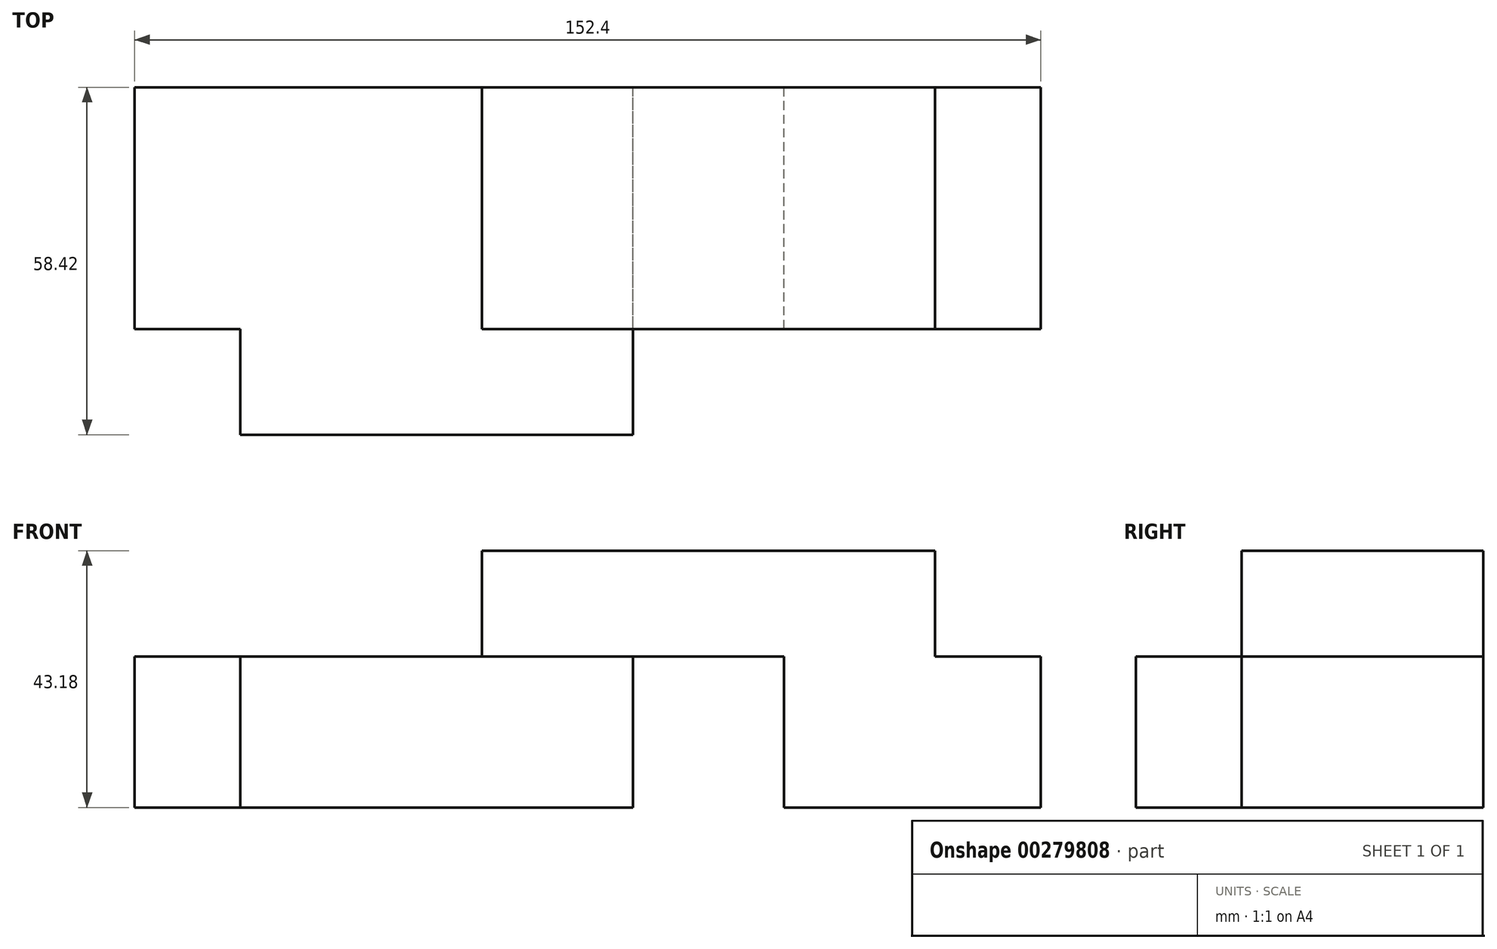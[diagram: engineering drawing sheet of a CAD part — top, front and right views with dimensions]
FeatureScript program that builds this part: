
annotation { "Feature Type Name" : "Feature", "Feature Type Description" : "" }
export const myFeature = defineFeature(function(context is Context, id is Id, definition is map)
    precondition{}
    {
        {
            var Q0;
            Q0=qCreatedBy(makeId("Right.planeOp"),FACE);
            var sketch = newSketch(context, id + "F0", { "sketchPlane" : qUnion([Q0])});
            skLineSegment(sketch, "E0.bottom", {"start": v(16.45, 25.4) * mm, "end": v(57.09, 25.4) * mm});
            skLineSegment(sketch, "E0.top", {"start": v(16.45, 0) * mm, "end": v(57.09, 0) * mm});
            skLineSegment(sketch, "E0.left", {"start": v(16.45, 25.4) * mm, "end": v(16.45, 0) * mm});
            skLineSegment(sketch, "E0.right", {"start": v(57.09, 25.4) * mm, "end": v(57.09, 0) * mm});
            skSolve(sketch);
        }
        {
            var Q0;
            Q0=makeQuery(id+"F0.imprint","IMPRINT",FACE,{"disambiguationData":[TD([[makeQuery(id+"F0.imprint","IMPRINT",EDGE,{"derivedFrom":sQuery(id+"F0.wireOp",EDGE,"E0.bottom")}),-1.0]])]});
            extrude(context, id + "F1", {"entities" : qUnion([Q0]), "depth" : 17.78 * mm});
        }
        {
            var Q0;
            Q0=makeQuery(id+"F1.opExtrude","CAP_FACE",FACE,{"disambiguationData":[OSD([sQuery(id+"F0.wireOp",EDGE,"E0.bottom"),sQuery(id+"F0.wireOp",EDGE,"E0.top"),sQuery(id+"F0.wireOp",EDGE,"E0.left"),sQuery(id+"F0.wireOp",EDGE,"E0.right")])],"isStart":true});
            extrude(context, id + "F2", {"entities" : qUnion([Q0]), "operationType" : NewBodyOperationType.ADD, "depth" : 25.4 * mm});
        }
        {
            var Q0;
            {var subQ0=sQuery(id+"F0.wireOp",EDGE,"E0.bottom");Q0=makeQuery(id+"F2.boolean.opBoolean","MERGE",FACE,{"derivedFrom":[makeQuery(id+"F1.opExtrude","SWEPT_FACE",FACE,{"disambiguationData":[OSD([subQ0])]}),makeQuery(id+"F2.opExtrude","SWEPT_FACE",FACE,{"disambiguationData":[OSD([subQ0])]})]});}
            var sketch = newSketch(context, id + "F3", { "sketchPlane" : qUnion([Q0])});
            skLineSegment(sketch, "E1", {"start": v(0, 57.09) * mm, "end": v(0, 16.45) * mm});
            skSolve(sketch);
        }
        {
            var Q0;
            {var subQ0=sQuery(id+"F3.wireOp",EDGE,"E1");Q0=makeQuery(id+"F3.imprint","IMPRINT",FACE,{"disambiguationData":[TD([[makeQuery(id+"F3.imprint","IMPRINT",EDGE,{"derivedFrom":subQ0}),-1.0]])]});}
            extrude(context, id + "F4", {"entities" : qUnion([Q0]), "operationType" : NewBodyOperationType.ADD, "depth" : 17.78 * mm});
        }
        {
            var Q0;
            {var subQ0=sQuery(id+"F0.wireOp",EDGE,"E0.bottom");Q0=makeQuery(id+"F4.boolean.opBoolean","MERGE",FACE,{"derivedFrom":[makeQuery(id+"F2.opExtrude","CAP_FACE",FACE,{"disambiguationData":[OSD([subQ0,sQuery(id+"F0.wireOp",EDGE,"E0.top"),sQuery(id+"F0.wireOp",EDGE,"E0.left"),sQuery(id+"F0.wireOp",EDGE,"E0.right")])],"isStart":false}),makeQuery(id+"F4.opExtrude","SWEPT_FACE",FACE,{"disambiguationData":[OSD([subQ0])]})]});}
            var sketch = newSketch(context, id + "F5", { "sketchPlane" : qUnion([Q0])});
            skLineSegment(sketch, "E2", {"start": v(-16.45, 25.4) * mm, "end": v(-57.09, 25.4) * mm});
            skSolve(sketch);
        }
        {
            var Q0;
            {var subQ0=sQuery(id+"F5.wireOp",EDGE,"E2");Q0=makeQuery(id+"F5.imprint","IMPRINT",FACE,{"disambiguationData":[TD([[makeQuery(id+"F5.imprint","IMPRINT",EDGE,{"derivedFrom":subQ0}),-1.0]])]});}
            extrude(context, id + "F6", {"entities" : qUnion([Q0]), "operationType" : NewBodyOperationType.ADD, "depth" : 50.8 * mm});
        }
        {
            var Q0;
            Q0=makeQuery(id+"F6.opExtrude","SWEPT_FACE",FACE,{"disambiguationData":[OSD([sQuery(id+"F5.wireOp",EDGE,"E2")])]});
            var sketch = newSketch(context, id + "F7", { "sketchPlane" : qUnion([Q0])});
            skLineSegment(sketch, "E3", {"start": v(-50.8, -16.45) * mm, "end": v(-50.8, -57.09) * mm});
            skSolve(sketch);
        }
        {
            var Q0;
            {var subQ0=sQuery(id+"F7.wireOp",EDGE,"E3");Q0=makeQuery(id+"F7.imprint","IMPRINT",FACE,{"disambiguationData":[TD([[makeQuery(id+"F7.imprint","IMPRINT",EDGE,{"derivedFrom":subQ0}),-1.0]])]});}
            extrude(context, id + "F8", {"entities" : qUnion([Q0]), "operationType" : NewBodyOperationType.ADD, "depth" : 25.4 * mm});
        }
        {
            var Q0;
            {var subQ0=sQuery(id+"F5.wireOp",EDGE,"E2");Q0=makeQuery(id+"F8.boolean.opBoolean","MERGE",FACE,{"derivedFrom":[makeQuery(id+"F6.opExtrude","CAP_FACE",FACE,{"disambiguationData":[OSD([sQuery(id+"F0.wireOp",EDGE,"E0.bottom"),sQuery(id+"F0.wireOp",EDGE,"E0.left"),sQuery(id+"F0.wireOp",EDGE,"E0.right"),subQ0])],"isStart":false}),makeQuery(id+"F8.opExtrude","SWEPT_FACE",FACE,{"disambiguationData":[OSD([subQ0])]})]});}
            var sketch = newSketch(context, id + "F9", { "sketchPlane" : qUnion([Q0])});
            skLineSegment(sketch, "E4", {"start": v(-57.09, 25.4) * mm, "end": v(-16.45, 25.4) * mm});
            skSolve(sketch);
        }
        {
            var Q0;
            {var subQ0=sQuery(id+"F9.wireOp",EDGE,"E4");Q0=makeQuery(id+"F9.imprint","IMPRINT",FACE,{"disambiguationData":[TD([[makeQuery(id+"F9.imprint","IMPRINT",EDGE,{"derivedFrom":subQ0}),-1.0]])]});}
            extrude(context, id + "F10", {"entities" : qUnion([Q0]), "operationType" : NewBodyOperationType.ADD, "depth" : 58.42 * mm});
        }
        {
            var Q0;
            {var subQ0=sQuery(id+"F5.wireOp",EDGE,"E2");var subQ1=sQuery(id+"F0.wireOp",EDGE,"E0.left");var subQ2=sQuery(id+"F0.wireOp",EDGE,"E0.bottom");Q0=makeQuery(id+"F10.boolean.opBoolean","MERGE",FACE,{"derivedFrom":[makeQuery(id+"F8.boolean.opBoolean","MERGE",FACE,{"derivedFrom":[makeQuery(id+"F6.boolean.opBoolean","MERGE",FACE,{"derivedFrom":[makeQuery(id+"F4.boolean.opBoolean","MERGE",FACE,{"derivedFrom":[makeQuery(id+"F2.boolean.opBoolean","MERGE",FACE,{"derivedFrom":[makeQuery(id+"F1.opExtrude","SWEPT_FACE",FACE,{"disambiguationData":[OSD([subQ1])]}),makeQuery(id+"F2.opExtrude","SWEPT_FACE",FACE,{"disambiguationData":[OSD([subQ1])]})]}),makeQuery(id+"F4.opExtrude","SWEPT_FACE",FACE,{"disambiguationData":[OSD([subQ2,subQ1])]})]}),makeQuery(id+"F6.opExtrude","SWEPT_FACE",FACE,{"disambiguationData":[OSD([subQ2,subQ1])]})]}),makeQuery(id+"F8.opExtrude","SWEPT_FACE",FACE,{"disambiguationData":[OSD([subQ2,subQ1,subQ0])]})]}),makeQuery(id+"F10.opExtrude","SWEPT_FACE",FACE,{"disambiguationData":[OSD([subQ2,subQ1,subQ0])]})]});}
            var sketch = newSketch(context, id + "F11", { "sketchPlane" : qUnion([Q0])});
            skLineSegment(sketch, "E5", {"start": v(-116.84, 25.4) * mm, "end": v(-116.84, 0) * mm});
            skLineSegment(sketch, "E6", {"start": v(-76.2, 25.4) * mm, "end": v(-50.8, 25.4) * mm});
            skSolve(sketch);
        }
        {
            var Q0;
            {var subQ5=sQuery(id+"F11.wireOp",EDGE,"E5");Q0=makeQuery(id+"F11.imprint","IMPRINT",FACE,{"disambiguationData":[TD([[makeQuery(id+"F11.imprint","IMPRINT",EDGE,{"derivedFrom":subQ5}),1.0]])]});}
            extrude(context, id + "F12", {"entities" : qUnion([Q0]), "operationType" : NewBodyOperationType.ADD, "depth" : 17.78 * mm});
        }
    });
